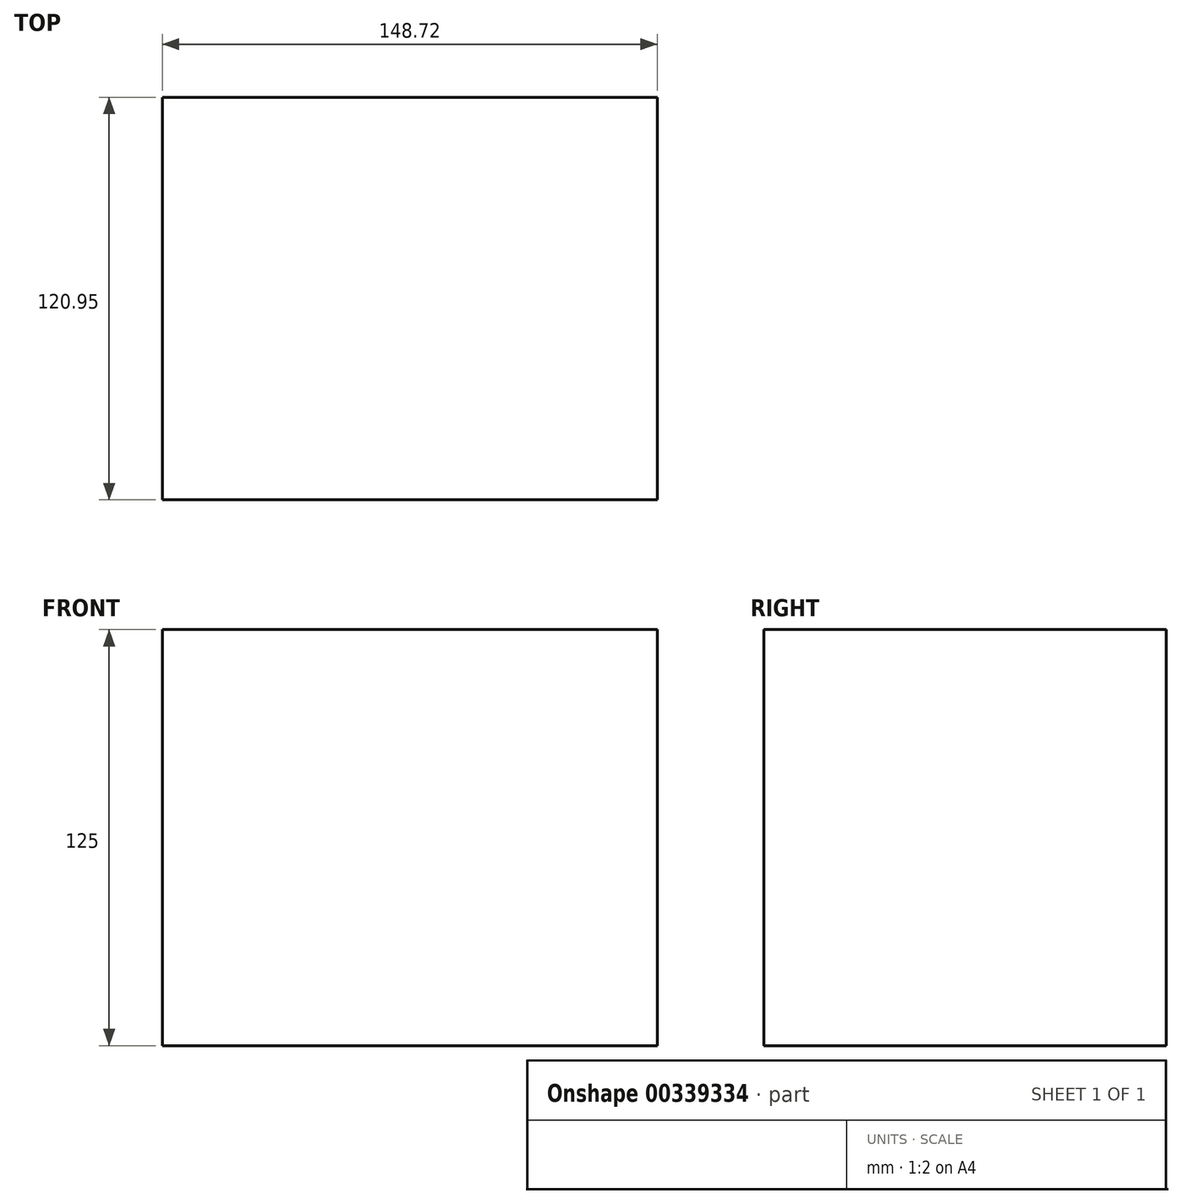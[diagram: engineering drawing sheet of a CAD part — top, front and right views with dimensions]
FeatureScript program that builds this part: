
annotation { "Feature Type Name" : "Feature", "Feature Type Description" : "" }
export const myFeature = defineFeature(function(context is Context, id is Id, definition is map)
    precondition{}
    {
        {
            var Q0;
            Q0=qCreatedBy(makeId("Top.planeOp"),FACE);
            var sketch = newSketch(context, id + "F0", { "sketchPlane" : qUnion([Q0])});
            skLineSegment(sketch, "E0.bottom", {"start": v(74.22, -74.78) * mm, "end": v(-74.5, -74.78) * mm});
            skLineSegment(sketch, "E0.top", {"start": v(74.22, 46.17) * mm, "end": v(-74.5, 46.17) * mm});
            skLineSegment(sketch, "E0.left", {"start": v(74.22, -74.78) * mm, "end": v(74.22, 46.17) * mm});
            skLineSegment(sketch, "E0.right", {"start": v(-74.5, -74.78) * mm, "end": v(-74.5, 46.17) * mm});
            skSolve(sketch);
        }
        {
            var Q0;
            Q0 = qSketchRegion(id + "F0", true);
            extrude(context, id + "F1", {"entities" : qUnion([Q0]), "depth" : 25 * mm});
        }
        {
            var Q0;
            Q0 = qSketchRegion(id + "F0", true);
            extrude(context, id + "F2", {"entities" : qUnion([Q0]), "operationType" : NewBodyOperationType.ADD, "oppositeDirection" : true, "depth" : 100 * mm});
        }
    });
